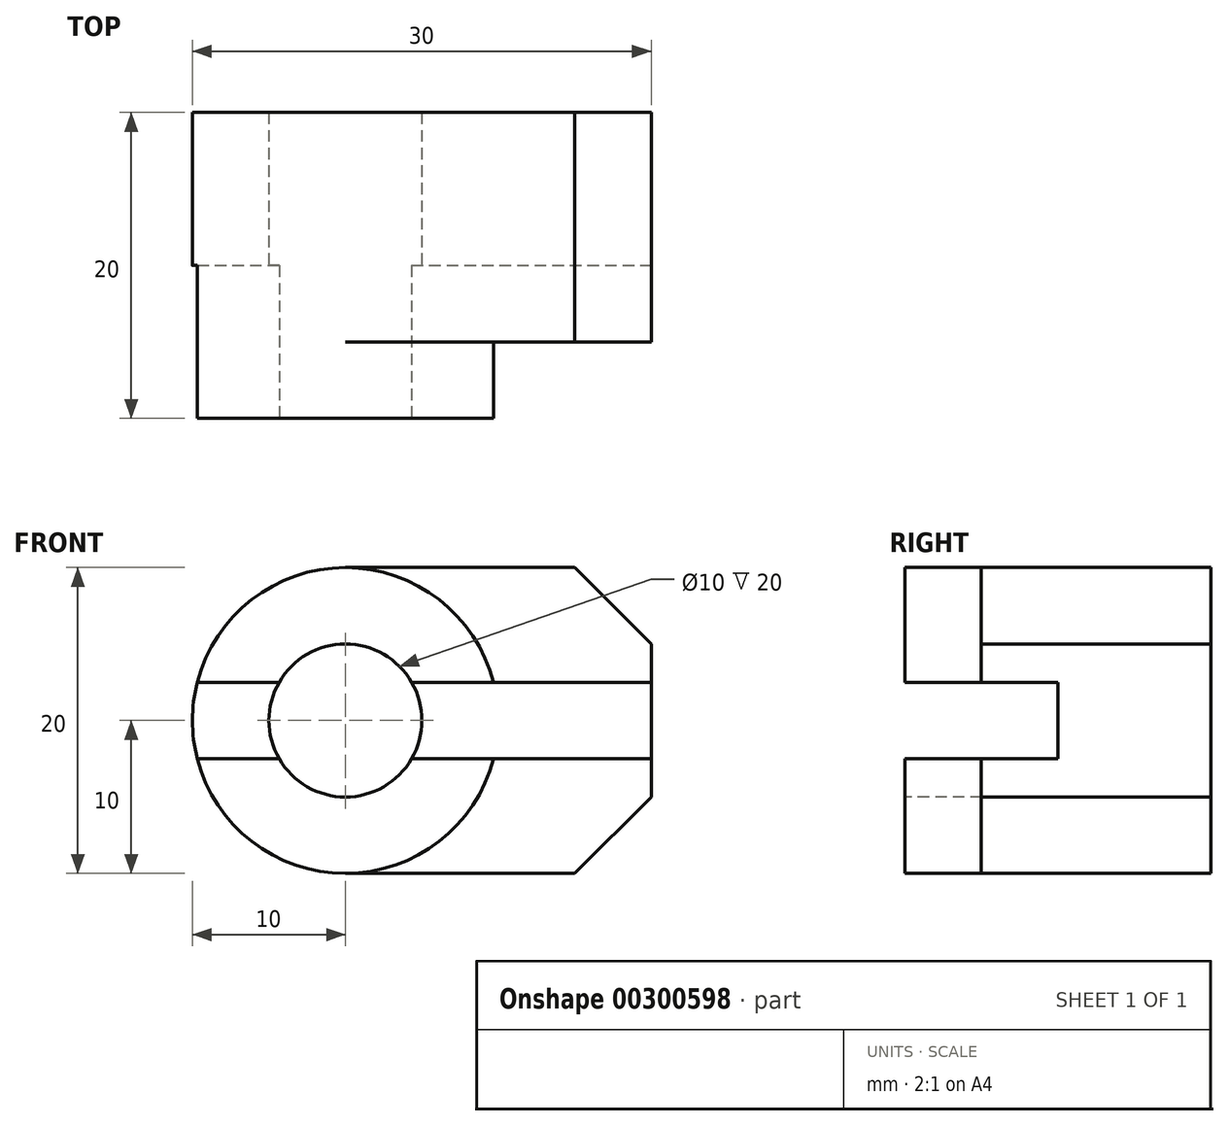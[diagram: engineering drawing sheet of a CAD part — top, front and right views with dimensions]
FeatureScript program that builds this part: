
annotation { "Feature Type Name" : "Feature", "Feature Type Description" : "" }
export const myFeature = defineFeature(function(context is Context, id is Id, definition is map)
    precondition{}
    {
        {
            var Q0;
            Q0=qCreatedBy(makeId("Front.planeOp"),FACE);
            var sketch = newSketch(context, id + "F0", { "sketchPlane" : qUnion([Q0])});
            skCircle(sketch, "E0", {"center": v(0, 0) * mm, "radius": 10 * mm});
            skSolve(sketch);
        }
        {
            var Q0;
            Q0 = qSketchRegion(id + "F0", true);
            extrude(context, id + "F1", {"entities" : qUnion([Q0]), "endBound" : BoundingType.SYMMETRIC, "depth" : 20 * mm});
        }
        {
            var Q0;
            Q0=qCreatedBy(makeId("Front.planeOp"),FACE);
            var sketch = newSketch(context, id + "F2", { "sketchPlane" : qUnion([Q0])});
            skLineSegment(sketch, "E1", {"start": v(0, 10) * mm, "end": v(15, 10) * mm});
            skLineSegment(sketch, "E2", {"start": v(15, 10) * mm, "end": v(20, 5) * mm});
            skLineSegment(sketch, "E3", {"start": v(0, 0) * mm, "end": v(29.92, 0) * mm, "construction": true});
            skLineSegment(sketch, "E4", {"start": v(20, 5) * mm, "end": v(20, 0) * mm});
            skLineSegment(sketch, "E5.MirrorCS", {"start": v(0, -10) * mm, "end": v(15, -10) * mm});
            skLineSegment(sketch, "E6.MirrorCS", {"start": v(15, -10) * mm, "end": v(20, -5) * mm});
            skLineSegment(sketch, "E7.MirrorCS", {"start": v(20, -5) * mm, "end": v(20, 0) * mm});
            skLineSegment(sketch, "E8", {"start": v(0, 10) * mm, "end": v(0, -10) * mm});
            skSolve(sketch);
        }
        {
            var Q0;
            Q0=makeQuery(id+"F2.imprint","IMPRINT",FACE,{"disambiguationData":[TD([[makeQuery(id+"F2.imprint","IMPRINT",EDGE,{"derivedFrom":sQuery(id+"F2.wireOp",EDGE,"E1")}),-1.0]])]});
            extrude(context, id + "F3", {"entities" : qUnion([Q0]), "operationType" : NewBodyOperationType.ADD, "oppositeDirection" : true, "depth" : 10 * mm, "hasSecondDirection" : true, "secondDirectionOppositeDirection" : false, "secondDirectionDepth" : 5 * mm});
        }
        {
            var Q0;
            Q0=makeQuery(id+"F1.opExtrude","CAP_FACE",FACE,{"disambiguationData":[OSD([sQuery(id+"F0.wireOp",EDGE,"E0")])],"isStart":false});
            var sketch = newSketch(context, id + "F4", { "sketchPlane" : qUnion([Q0])});
            skCircle(sketch, "E9", {"center": v(0, 0) * mm, "radius": 5 * mm});
            skSolve(sketch);
        }
        {
            var Q0;
            Q0 = qSketchRegion(id + "F4", true);
            extrude(context, id + "F5", {"entities" : qUnion([Q0]), "operationType" : NewBodyOperationType.REMOVE, "endBound" : BoundingType.THROUGH_ALL, "oppositeDirection" : true, "depth" : 25 * mm});
        }
        {
            var Q0;
            Q0=qCreatedBy(makeId("Front.planeOp"),FACE);
            var sketch = newSketch(context, id + "F6", { "sketchPlane" : qUnion([Q0])});
            skLineSegment(sketch, "E10", {"start": v(-14.03, 0) * mm, "end": v(24.23, 0) * mm, "construction": true});
            skLineSegment(sketch, "E11", {"start": v(-10, 0) * mm, "end": v(-10, 2.5) * mm});
            skLineSegment(sketch, "E12", {"start": v(20, 2.5) * mm, "end": v(20, 0) * mm});
            skLineSegment(sketch, "E13.MirrorCS", {"start": v(20, -2.5) * mm, "end": v(20, 0) * mm});
            skLineSegment(sketch, "E14", {"start": v(-10, 2.5) * mm, "end": v(20, 2.5) * mm});
            skLineSegment(sketch, "E15.MirrorCS", {"start": v(-10, -2.5) * mm, "end": v(20, -2.5) * mm});
            skLineSegment(sketch, "E16.MirrorCS", {"start": v(-10, 0) * mm, "end": v(-10, -2.5) * mm});
            skSolve(sketch);
        }
        {
            var Q0;
            Q0 = qSketchRegion(id + "F6", true);
            extrude(context, id + "F7", {"entities" : qUnion([Q0]), "operationType" : NewBodyOperationType.REMOVE, "depth" : 10 * mm});
        }
    });
